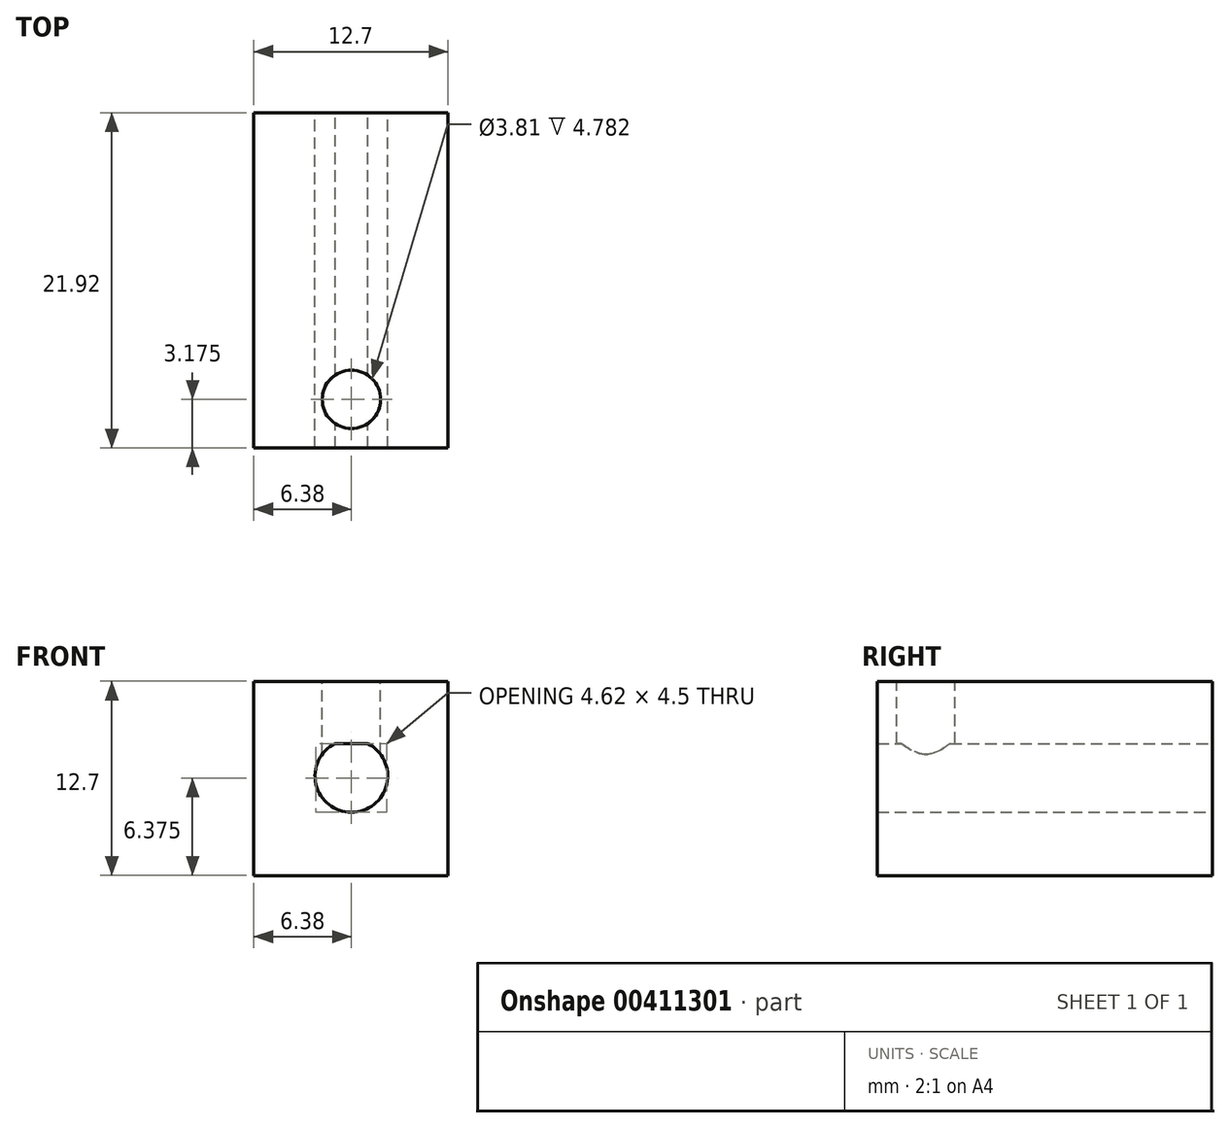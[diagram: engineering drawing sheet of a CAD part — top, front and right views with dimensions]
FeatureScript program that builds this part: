
annotation { "Feature Type Name" : "Feature", "Feature Type Description" : "" }
export const myFeature = defineFeature(function(context is Context, id is Id, definition is map)
    precondition{}
    {
        {
            var Q0;
            Q0=qCreatedBy(makeId("Front.planeOp"),FACE);
            var sketch = newSketch(context, id + "F0", { "sketchPlane" : qUnion([Q0])});
            skLineSegment(sketch, "E0.bottom", {"start": v(-6.38, 6.2) * mm, "end": v(6.32, 6.2) * mm});
            skLineSegment(sketch, "E0.top", {"start": v(-6.38, -6.5) * mm, "end": v(6.32, -6.5) * mm});
            skLineSegment(sketch, "E0.left", {"start": v(-6.38, 6.2) * mm, "end": v(-6.38, -6.5) * mm});
            skLineSegment(sketch, "E0.right", {"start": v(6.32, 6.2) * mm, "end": v(6.32, -6.5) * mm});
            skArc(sketch, "E1", {"start": v(-1.06, 2.13) * mm, "mid": v(0, -2.38) * mm, "end": v(1.06, 2.13) * mm});
            skLineSegment(sketch, "E2", {"start": v(-1.06, 2.13) * mm, "end": v(1.06, 2.13) * mm});
            skSolve(sketch);
        }
        {
            var Q0;
            Q0=makeQuery(id+"F0.imprint","IMPRINT",FACE,{"disambiguationData":[TD([[makeQuery(id+"F0.imprint","IMPRINT",EDGE,{"derivedFrom":sQuery(id+"F0.wireOp",EDGE,"E0.bottom")}),-1.0]])]});
            extrude(context, id + "F1", {"entities" : qUnion([Q0]), "depth" : 21.92 * mm});
        }
        {
            var Q0;
            Q0=makeQuery(id+"F1.opExtrude","SWEPT_FACE",FACE,{"disambiguationData":[OSD([sQuery(id+"F0.wireOp",EDGE,"E0.bottom")])]});
            var sketch = newSketch(context, id + "F2", { "sketchPlane" : qUnion([Q0])});
            skCircle(sketch, "E3", {"center": v(0, -18.75) * mm, "radius": 1.9 * mm});
            skLineSegment(sketch, "E4", {"start": v(0, 0) * mm, "end": v(0, -16.84) * mm, "construction": true});
            skPoint(sketch, "E5", {"position": v(0, -21.92) * mm});
            skSolve(sketch);
        }
        {
            var Q0;
            Q0=makeQuery(id+"F2.imprint","IMPRINT",FACE,{"disambiguationData":[TD([[makeQuery(id+"F2.imprint","IMPRINT",EDGE,{"derivedFrom":sQuery(id+"F2.wireOp",EDGE,"E3")}),1.0]])]});
            extrude(context, id + "F3", {"entities" : qUnion([Q0]), "operationType" : NewBodyOperationType.REMOVE, "oppositeDirection" : true, "depth" : 6.35 * mm});
        }
    });
